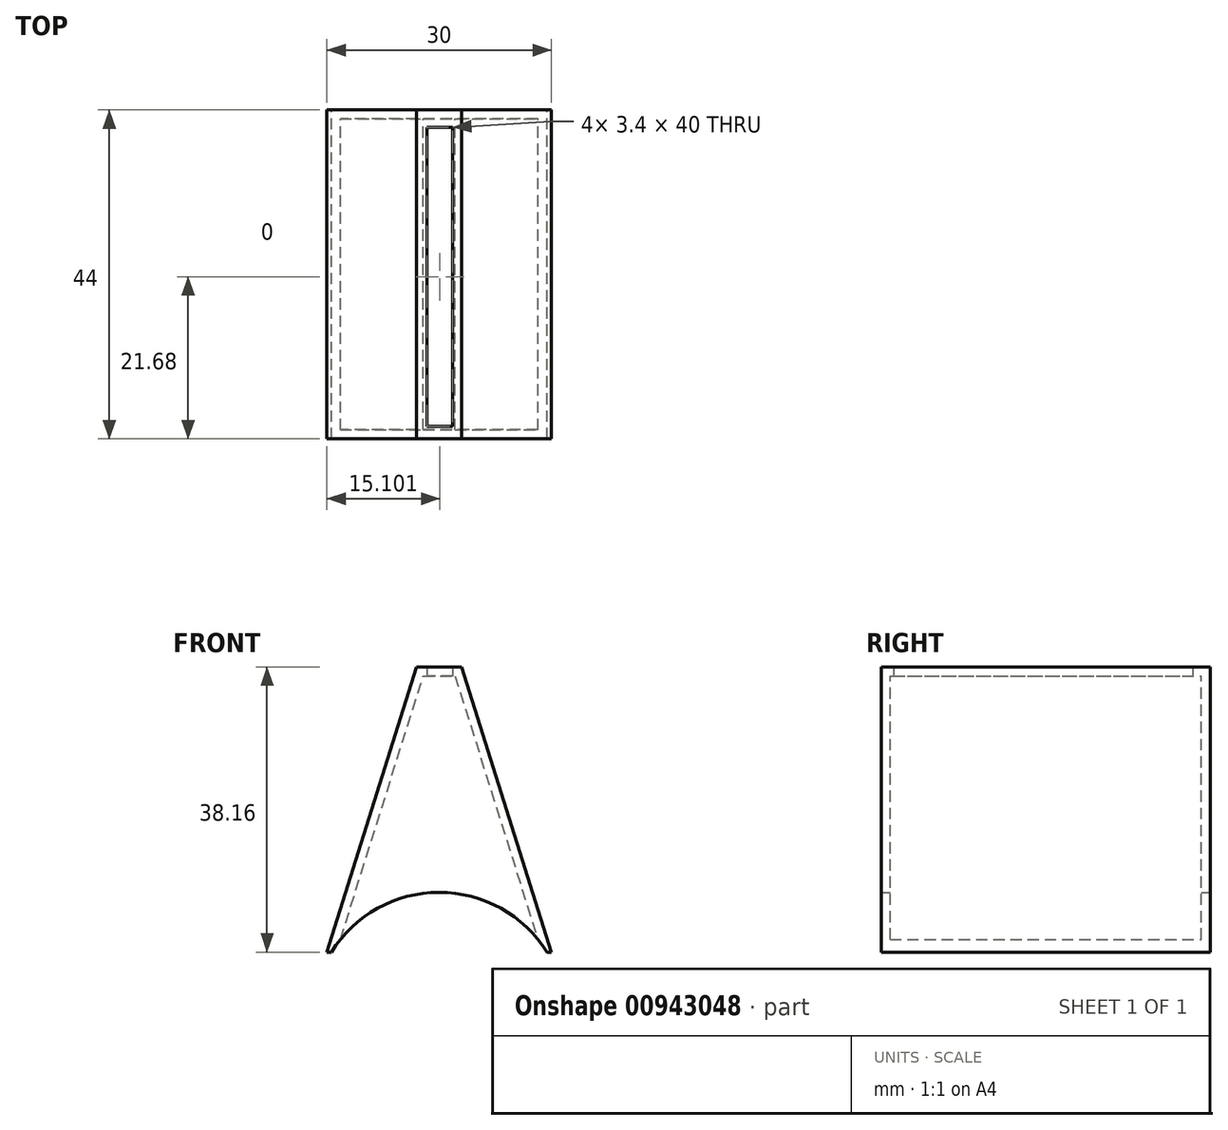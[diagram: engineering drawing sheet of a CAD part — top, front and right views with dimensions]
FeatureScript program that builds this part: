
annotation { "Feature Type Name" : "Feature", "Feature Type Description" : "" }
export const myFeature = defineFeature(function(context is Context, id is Id, definition is map)
    precondition{}
    {
        {
            var Q0;
            Q0=qCreatedBy(makeId("Front.planeOp"),FACE);
            var sketch = newSketch(context, id + "F0", { "sketchPlane" : qUnion([Q0])});
            skLineSegment(sketch, "E0", {"start": v(-15, 0) * mm, "end": v(-3, 38.16) * mm});
            skLineSegment(sketch, "E1", {"start": v(-3, 38.16) * mm, "end": v(3, 38.16) * mm});
            skLineSegment(sketch, "E2", {"start": v(3, 38.16) * mm, "end": v(15, 0) * mm});
            skLineSegment(sketch, "E3", {"start": v(-15, 0) * mm, "end": v(15, 0) * mm});
            skSolve(sketch);
        }
        {
            var Q0;
            Q0 = qSketchRegion(id + "F0", true);
            extrude(context, id + "F1", {"entities" : qUnion([Q0]), "depth" : 44 * mm, "offsetDistance" : 25 * mm});
        }
        {
            var Q0;
            Q0=qCreatedBy(makeId("Front.planeOp"),FACE);
            cPlane(context, id + "F2", {"entities" : qUnion([Q0]), "cplaneType" : CPlaneType.OFFSET, "offset" : 25 * mm, "width" : 150 * mm, "height" : 150 * mm});
        }
        {
            var Q0;
            Q0=qCreatedBy(id+"F2.planeOp",FACE);
            var sketch = newSketch(context, id + "F3", { "sketchPlane" : qUnion([Q0])});
            skCircle(sketch, "E4", {"center": v(0, -9) * mm, "radius": 17 * mm});
            skSolve(sketch);
        }
        {
            var Q0;
            Q0=makeQuery(id+"F1.opExtrude","SWEPT_FACE",FACE,{"disambiguationData":[OSD([sQuery(id+"F0.wireOp",EDGE,"E3")])]});
            shell(context, id + "F4", {"entities" : qUnion([Q0]), "thickness" : 1.2 * mm});
        }
        {
            var Q0;
            Q0 = qSketchRegion(id + "F3", true);
            extrude(context, id + "F5", {"entities" : qUnion([Q0]), "operationType" : NewBodyOperationType.REMOVE, "endBound" : BoundingType.SYMMETRIC, "depth" : 50 * mm, "offsetDistance" : 25 * mm});
        }
        {
            var Q0;
            Q0=qCreatedBy(makeId("Top.planeOp"),FACE);
            var sketch = newSketch(context, id + "F6", { "sketchPlane" : qUnion([Q0])});
            skLineSegment(sketch, "E5.bottom", {"start": v(-1.6, -2.32) * mm, "end": v(1.8, -2.32) * mm});
            skLineSegment(sketch, "E5.top", {"start": v(-1.6, -42.32) * mm, "end": v(1.8, -42.32) * mm});
            skLineSegment(sketch, "E5.left", {"start": v(-1.6, -2.32) * mm, "end": v(-1.6, -42.32) * mm});
            skLineSegment(sketch, "E5.right", {"start": v(1.8, -2.32) * mm, "end": v(1.8, -42.32) * mm});
            skSolve(sketch);
        }
        {
            var Q0;
            Q0 = qSketchRegion(id + "F6", true);
            extrude(context, id + "F7", {"entities" : qUnion([Q0]), "operationType" : NewBodyOperationType.REMOVE, "depth" : 50 * mm, "offsetDistance" : 25 * mm});
        }
    });
